# Revit family: Поли-Групп_ЗадвижкаШибернаяEAZ-ZT_DN50-500
name_source: partatom
category: Арматура трубопроводов
units: mm (PartAtom-declared; Revit-internal decimal feet)

## family parameters
Всегда вертикально = Нет
На основе рабочей плоскости = Нет
Общий = Нет
При загрузке вырезать с полостями = Нет
Размер круглого соединителя = Использовать диаметр
Тип детали = Клапан - Вставляется

## types (8) — shared parameters
ADSK_URL страницы изделия = https://www.polycorr.ru
ADSK_Версия Revit = 2019
ADSK_Единица измерения = шт
ADSK_Завод-изготовитель = ООО ПК «Поли-Групп»
ADSK_Материал = Высокопрочный чугун GGG-40
ADSK_Материал наименование = Высокопрочный чугун с шаровидным графитом (GGG-40)
Kv = 1.00 м³/ч
r = 10 мм
Класс герметичности = А по ГОСТ Р 9544-2015
Материал Диска = Нержавеющая сталь марки 08Х18Н10
Материал Ножа = Сталь нержавеющая
Материал Рамы = Сталь синий
Материал уплотнителя = NBR
Назначение = Для установки в качестве запорного устройства на трубопроводах
Нож_t = 8 мм
Покрытие = Высококачественное эпоксидное покрытие толщиной 300 мкм
Рабочая среда = Техническая вода, канализационные стоки, морская вода
Разработчик = https://3dbim.pro
Рама_t = 3 мм
Срок службы = 50 лет
ТВ = Поли-Групп_ЗадвижкаШибернаяEAZ-ZT_DN50-500
Температура рабочей среды = 0 до +70°С
Тип привода = Штурвал
Тип присоединения = Межфланцевое
zero-valued in all types: Крутящий момент

## per-type parameters (varying)
- 50-10: ADSK_Марка=EAZ-KV-1 DN50 PN10; ADSK_Масса=4.95; ADSK_Масса_Текст=4.95; ADSK_Наименование=Задвижка шиберно-ножевая EAZ ZT для сточных вод межфланцевая DN50 PN10; ADSK_Наименование краткое=Задвижка шиберно-ножевая EAZ ZT DN50 PN10; D1=125 мм; DN=50 мм; DO=180 мм; E=136 мм; H1=70 мм; H2=242 мм; H3=110 мм; L=40 мм; L1=17 мм; O=80 мм; PN=10.0 бары; XXL=5 мм; d=16 мм; k=125 мм; r1=13 мм; r2=18 мм; Габаритные размеры=40х312х180; Гайка_Высота=24 мм; Гайка_Ширина=32 мм; Нож_Выступ=22 мм; Подшипник_d=32 мм; Рама_h=87 мм; Стойка_t=19 мм; Стойка_Длина=80 мм; Шток_d=16 мм; Шток_Смещение=20 мм; Штурвал_Высота=45 мм
- 100-10: ADSK_Марка=EAZ-KV-1 DN100 PN10; ADSK_Масса=10.5; ADSK_Масса_Текст=10.5; ADSK_Наименование=Задвижка шиберно-ножевая EAZ ZT для сточных вод межфланцевая DN100 PN10; ADSK_Наименование краткое=Задвижка шиберно-ножевая EAZ ZT DN100 PN10; D1=160 мм; DN=100 мм; DO=200 мм; E=196 мм; H1=100 мм; H2=310 мм; H3=138 мм; L=50 мм; L1=22 мм; O=92 мм; PN=10.0 бары; XXL=35 мм; d=16 мм; k=180 мм; r1=15 мм; r2=21 мм; Габаритные размеры=50х410х200; Гайка_Высота=30 мм; Гайка_Ширина=40 мм; Нож_Выступ=31 мм; Подшипник_d=40 мм; Рама_h=122 мм; Стойка_t=25 мм; Стойка_Длина=92 мм; Шток_d=20 мм; Шток_Смещение=23 мм; Штурвал_Высота=50 мм
- 150-10: ADSK_Марка=EAZ-KV-1 DN150 PN10; ADSK_Масса=19.5; ADSK_Масса_Текст=19.5; ADSK_Наименование=Задвижка шиберно-ножевая EAZ ZT для сточных вод межфланцевая DN150 PN10; ADSK_Наименование краткое=Задвижка шиберно-ножевая EAZ ZT DN150 PN10; D1=240 мм; DN=150 мм; DO=250 мм; E=260 мм; H1=130 мм; H2=452 мм; H3=175 мм; L=60 мм; L1=26 мм; O=106 мм; PN=10.0 бары; XXL=65 мм; d=20 мм; k=240 мм; r1=19 мм; r2=26 мм; Габаритные размеры=60х582х250; Гайка_Высота=36 мм; Гайка_Ширина=48 мм; Нож_Выступ=54 мм; Подшипник_d=48 мм; Рама_h=215 мм; Стойка_t=36 мм; Стойка_Длина=106 мм; Шток_d=24 мм; Шток_Смещение=27 мм; Штурвал_Высота=63 мм
- 200-10: ADSK_Марка=EAZ-KV-1 DN200 PN10; ADSK_Масса=29.9; ADSK_Масса_Текст=29.9; ADSK_Наименование=Задвижка шиберно-ножевая EAZ ZT для сточных вод межфланцевая DN200 PN10; ADSK_Наименование краткое=Задвижка шиберно-ножевая EAZ ZT DN200 PN10; D1=295 мм; DN=200 мм; DO=280 мм; E=317 мм; H1=160 мм; H2=553 мм; H3=205 мм; L=60 мм; L1=28 мм; O=126 мм; PN=10.0 бары; XXL=95 мм; d=20 мм; k=295 мм; r1=18 мм; r2=25 мм; Габаритные размеры=60х713х280; Гайка_Высота=36 мм; Гайка_Ширина=48 мм; Нож_Выступ=70 мм; Подшипник_d=48 мм; Рама_h=278 мм; Стойка_t=44 мм; Стойка_Длина=126 мм; Шток_d=24 мм; Шток_Смещение=32 мм; Штурвал_Высота=70 мм
- 250-10: ADSK_Марка=EAZ-KV-1 DN250 PN10; ADSK_Масса=47.9; ADSK_Масса_Текст=47.9; ADSK_Наименование=Задвижка шиберно-ножевая EAZ ZT для сточных вод межфланцевая DN250 PN10; ADSK_Наименование краткое=Задвижка шиберно-ножевая EAZ ZT DN250 PN10; D1=350 мм; DN=250 мм; DO=320 мм; E=382 мм; H1=200 мм; H2=660 мм; H3=237 мм; L=70 мм; L1=33 мм; O=140 мм; PN=10.0 бары; XXL=135 мм; d=20 мм; k=350 мм; r1=18 мм; r2=25 мм; Габаритные размеры=70х860х320; Гайка_Высота=39 мм; Гайка_Ширина=52 мм; Нож_Выступ=86 мм; Подшипник_d=52 мм; Рама_h=343 мм; Стойка_t=53 мм; Стойка_Длина=140 мм; Шток_d=26 мм; Шток_Смещение=35 мм; Штурвал_Высота=80 мм
- 300-10: ADSK_Марка=EAZ-KV-1 DN300 PN10; ADSK_Масса=57.6; ADSK_Масса_Текст=57.6; ADSK_Наименование=Задвижка шиберно-ножевая EAZ ZT для сточных вод межфланцевая DN300 PN10; ADSK_Наименование краткое=Задвижка шиберно-ножевая EAZ ZT DN300 PN10; D1=400 мм; DN=300 мм; DO=400 мм; E=430 мм; H1=225 мм; H2=783 мм; H3=280 мм; L=70 мм; L1=38 мм; O=150 мм; PN=10.0 бары; XXL=160 мм; d=20 мм; k=400 мм; r1=18 мм; r2=25 мм; Габаритные размеры=70х1008х400; Гайка_Высота=42 мм; Гайка_Ширина=56 мм; Нож_Выступ=101 мм; Подшипник_d=56 мм; Рама_h=403 мм; Стойка_t=63 мм; Стойка_Длина=150 мм; Шток_d=28 мм; Шток_Смещение=38 мм; Штурвал_Высота=100 мм
- 400-8: ADSK_Марка=EAZ-KV-1 DN400 PN10; ADSK_Масса=145; ADSK_Масса_Текст=145; ADSK_Наименование=Задвижка шиберно-ножевая EAZ ZT для сточных вод межфланцевая DN400 PN8; ADSK_Наименование краткое=Задвижка шиберно-ножевая EAZ ZT DN400 PN8; D1=515 мм; DN=400 мм; DO=305 мм; E=580 мм; H1=290 мм; H2=1060 мм; H3=425 мм; L=100 мм; L1=58 мм; O=184 мм; PN=8.0 бары; XXL=225 мм; d=24 мм; k=515 мм; r1=19 мм; r2=26 мм; Габаритные размеры=100х1350х305; Гайка_Высота=48 мм; Гайка_Ширина=64 мм; Нож_Выступ=140 мм; Подшипник_d=64 мм; Рама_h=559 мм; Стойка_t=85 мм; Стойка_Длина=184 мм; Шток_d=32 мм; Шток_Смещение=46 мм; Штурвал_Высота=76 мм
- 500-8: ADSK_Марка=EAZ-KV-1 DN500 PN8; ADSK_Масса=225; ADSK_Масса_Текст=225; ADSK_Наименование=Задвижка шиберно-ножевая EAZ ZT для сточных вод межфланцевая DN500 PN8; ADSK_Наименование краткое=Задвижка шиберно-ножевая EAZ ZT DN500 PN8; D1=620 мм; DN=500 мм; DO=410 мм; E=730 мм; H1=340 мм; H2=1310 мм; H3=570 мм; L=110 мм; L1=76 мм; O=218 мм; PN=8.0 бары; XXL=275 мм; d=24 мм; k=630 мм; r1=20 мм; r2=28 мм; Габаритные размеры=110х1650х410; Гайка_Высота=54 мм; Гайка_Ширина=72 мм; Нож_Выступ=159 мм; Подшипник_d=72 мм; Рама_h=638 мм; Стойка_t=105 мм; Стойка_Длина=218 мм; Шток_d=36 мм; Шток_Смещение=55 мм; Штурвал_Высота=103 мм
